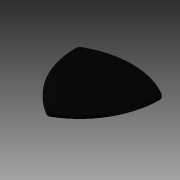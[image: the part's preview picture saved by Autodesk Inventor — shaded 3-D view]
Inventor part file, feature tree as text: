
AUTODESK INVENTOR PART (.ipt)
format: ipt  version: 2013 (Build 170138000, 138)  size: 108,544 bytes
history: native  units: mm
features: extrude x2, sketch x2
ambient origin geometry x8: Origin, YZ Plane, XZ Plane, XY Plane, X Axis, Y Axis, Z Axis, Center Point
bodies: Solid1 (feature_tree)
feature tree (4):
  extrude  "Extrusion1"  Depth=250.0mm
  extrude  "Extrusion2"  Depth=9.525mm TaperAngle=0.0deg
  sketch  "Sketch1"  dims[d0=200.0mm d2=250.0mm]
  sketch  "Sketch2"  dims[d3=12.5mm d4=9.525mm d5=0.0mm d6=8.2mm d8=5.0mm d9=0.0mm]
